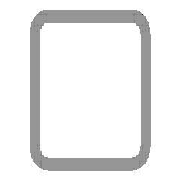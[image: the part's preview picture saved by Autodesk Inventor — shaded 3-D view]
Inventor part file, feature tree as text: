
AUTODESK INVENTOR PART (.ipt)
format: ipt  version: 2021 (Build 250183000, 183)  size: 140,288 bytes
history: native  units: mm (DEFAULTED — no unit token found)
features: other x5, sketch x3, extrude x1, split x1, plane x1
ambient origin geometry x8: Origin, YZ Plane, XZ Plane, XY Plane, X Axis, Y Axis, Z Axis, Center Point
bodies: Solid1 (feature_tree)
feature tree (11):
  parser-record x1  (decoder bookkeeping rows leaked as tree rows — omitted from the tree; the rows remain in map.json)
  other  "Driven Length"
  other  "Plano inicial"
  other  "Plano final"
  extrude  "Corpo"  TaperAngle=0.0deg  [1 undecoded]
  other  "Plano de trabalho4"
  split  "Dividir1"
  sketch  "Esboço"  dims[d11=50.8mm d12=4.7625mm d13=-0.0mm d14=1033.450655mm d15=25.4mm d16=25.4mm d17=9.525mm d18=90.0deg d19=1033.450655mm]
  sketch  "Sketch3"  dims[d3=1030.79861mm d4=0.0mm]
  plane  "Work Plane3"
  sketch  "Sketch4"  dims[d10=50.8mm]
note: 1 required parameter value undecoded (feature->parameter linkage not recoverable at this tier; creation-order binding heuristic only, values carry confidence <= 0.55)
